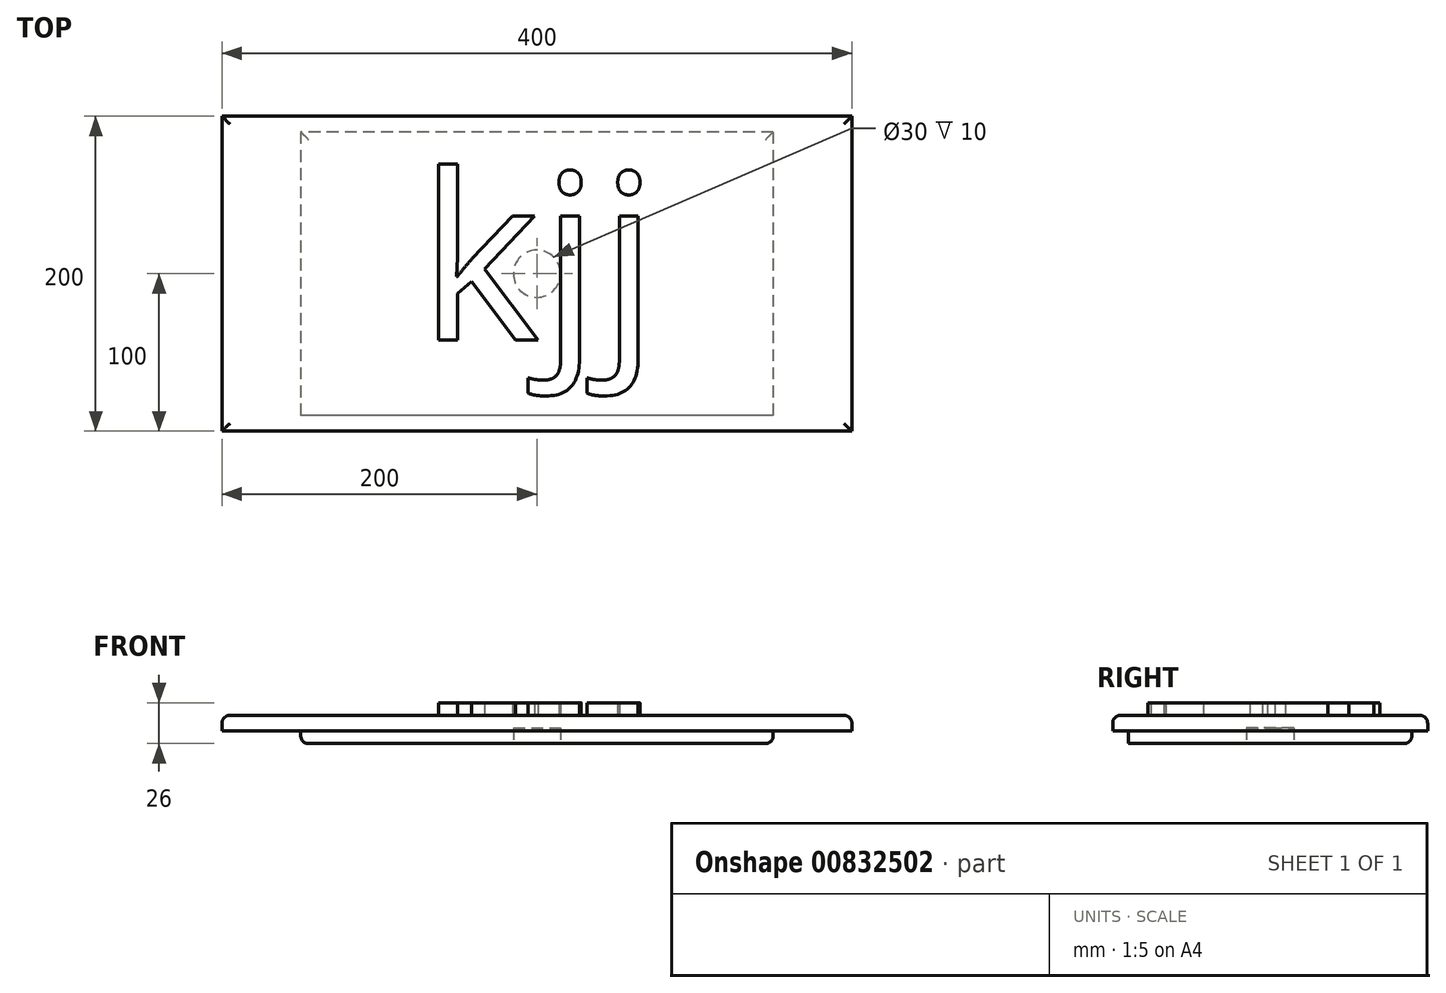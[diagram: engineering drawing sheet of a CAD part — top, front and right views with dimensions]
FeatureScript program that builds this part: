
annotation { "Feature Type Name" : "Feature", "Feature Type Description" : "" }
export const myFeature = defineFeature(function(context is Context, id is Id, definition is map)
    precondition{}
    {
        {
            var Q0;
            Q0=qCreatedBy(makeId("Top.planeOp"),FACE);
            var sketch = newSketch(context, id + "F0", { "sketchPlane" : qUnion([Q0])});
            skLineSegment(sketch, "E0.bottom", {"start": v(-200, 100) * mm, "end": v(200, 100) * mm});
            skLineSegment(sketch, "E0.top", {"start": v(-200, -100) * mm, "end": v(200, -100) * mm});
            skLineSegment(sketch, "E0.left", {"start": v(-200, 100) * mm, "end": v(-200, -100) * mm});
            skLineSegment(sketch, "E0.right", {"start": v(200, 100) * mm, "end": v(200, -100) * mm});
            skSolve(sketch);
        }
        {
            var Q0;
            Q0=makeQuery(id+"F0.imprint","IMPRINT",FACE,{"disambiguationData":[TD([[makeQuery(id+"F0.imprint","IMPRINT",EDGE,{"derivedFrom":sQuery(id+"F0.wireOp",EDGE,"E0.bottom")}),-1.0]])]});
            extrude(context, id + "F1", {"entities" : qUnion([Q0]), "depth" : 10 * mm, "offsetDistance" : 25 * mm});
        }
        {
            var Q0;
            Q0=qCreatedBy(makeId("Top.planeOp"),FACE);
            var sketch = newSketch(context, id + "F2", { "sketchPlane" : qUnion([Q0])});
            skLineSegment(sketch, "E1.bottom", {"start": v(150, 90) * mm, "end": v(-150, 90) * mm});
            skLineSegment(sketch, "E1.top", {"start": v(150, -90) * mm, "end": v(-150, -90) * mm});
            skLineSegment(sketch, "E1.left", {"start": v(150, 90) * mm, "end": v(150, -90) * mm});
            skLineSegment(sketch, "E1.right", {"start": v(-150, 90) * mm, "end": v(-150, -90) * mm});
            skSolve(sketch);
        }
        {
            var Q0;
            Q0=makeQuery(id+"F2.imprint","IMPRINT",FACE,{"disambiguationData":[TD([[makeQuery(id+"F2.imprint","IMPRINT",EDGE,{"derivedFrom":sQuery(id+"F2.wireOp",EDGE,"E1.bottom")}),1.0]])]});
            extrude(context, id + "F3", {"entities" : qUnion([Q0]), "operationType" : NewBodyOperationType.ADD, "oppositeDirection" : true, "depth" : 8 * mm, "offsetDistance" : 25 * mm});
        }
        {
            var Q0;
            Q0=makeQuery(id+"F1.opExtrude","CAP_FACE",FACE,{"disambiguationData":[OSD([sQuery(id+"F0.wireOp",EDGE,"E0.bottom"),sQuery(id+"F0.wireOp",EDGE,"E0.top"),sQuery(id+"F0.wireOp",EDGE,"E0.left"),sQuery(id+"F0.wireOp",EDGE,"E0.right")])],"isStart":false});
            fillet(context, id + "F4", {"entities" : qUnion([Q0]), "radius" : 5 * mm, "tangentPropagation" : true, "allowEdgeOverflow" : false});
        }
        {
            var Q0;
            Q0=makeQuery(id+"F3.opExtrude","CAP_EDGE",EDGE,{"disambiguationData":[OSD([sQuery(id+"F2.wireOp",EDGE,"E1.right")])],"isStart":false});
            var Q1;
            Q1=makeQuery(id+"F3.opExtrude","CAP_EDGE",EDGE,{"disambiguationData":[OSD([sQuery(id+"F2.wireOp",EDGE,"E1.bottom")])],"isStart":false});
            var Q2;
            Q2=makeQuery(id+"F3.opExtrude","CAP_EDGE",EDGE,{"disambiguationData":[OSD([sQuery(id+"F2.wireOp",EDGE,"E1.left")])],"isStart":false});
            fillet(context, id + "F5", {"entities" : qUnion([Q0, Q1, Q2]), "radius" : 5 * mm, "tangentPropagation" : true, "allowEdgeOverflow" : false});
        }
        {
            var Q0;
            Q0=makeQuery(id+"F1.opExtrude","CAP_FACE",FACE,{"disambiguationData":[OSD([sQuery(id+"F0.wireOp",EDGE,"E0.bottom"),sQuery(id+"F0.wireOp",EDGE,"E0.top"),sQuery(id+"F0.wireOp",EDGE,"E0.left"),sQuery(id+"F0.wireOp",EDGE,"E0.right")])],"isStart":false});
            var sketch = newSketch(context, id + "F6", { "sketchPlane" : qUnion([Q0])});
            skText(sketch, "E2", { "text": "kjj", "fontName": "OpenSans-Regular.ttf"});
            const initialGuessF6  = {"E2": [-0.075, -0.04226, 1, 0, 0.10614]};
            skSetInitialGuess(sketch, initialGuessF6);
            skSolve(sketch);
        }
        {
            var Q0;
            Q0 = qSketchRegion(id + "F6", true);
            extrude(context, id + "F7", {"entities" : qUnion([Q0]), "operationType" : NewBodyOperationType.ADD, "depth" : 8 * mm, "offsetDistance" : 25 * mm});
        }
        {
            var Q0;
            Q0=makeQuery(id+"F3.opExtrude","CAP_FACE",FACE,{"disambiguationData":[OSD([sQuery(id+"F2.wireOp",EDGE,"E1.bottom"),sQuery(id+"F2.wireOp",EDGE,"E1.top"),sQuery(id+"F2.wireOp",EDGE,"E1.left"),sQuery(id+"F2.wireOp",EDGE,"E1.right")])],"isStart":false});
            var sketch = newSketch(context, id + "F8", { "sketchPlane" : qUnion([Q0])});
            skCircle(sketch, "E3", {"center": v(0, 0) * mm, "radius": 15 * mm});
            skSolve(sketch);
        }
        {
            var Q0;
            Q0=makeQuery(id+"F8.imprint","IMPRINT",FACE,{"disambiguationData":[TD([[makeQuery(id+"F8.imprint","IMPRINT",EDGE,{"derivedFrom":sQuery(id+"F8.wireOp",EDGE,"E3")}),1.0]])]});
            extrude(context, id + "F9", {"entities" : qUnion([Q0]), "operationType" : NewBodyOperationType.REMOVE, "oppositeDirection" : true, "depth" : 10 * mm, "offsetDistance" : 25 * mm});
        }
    });
